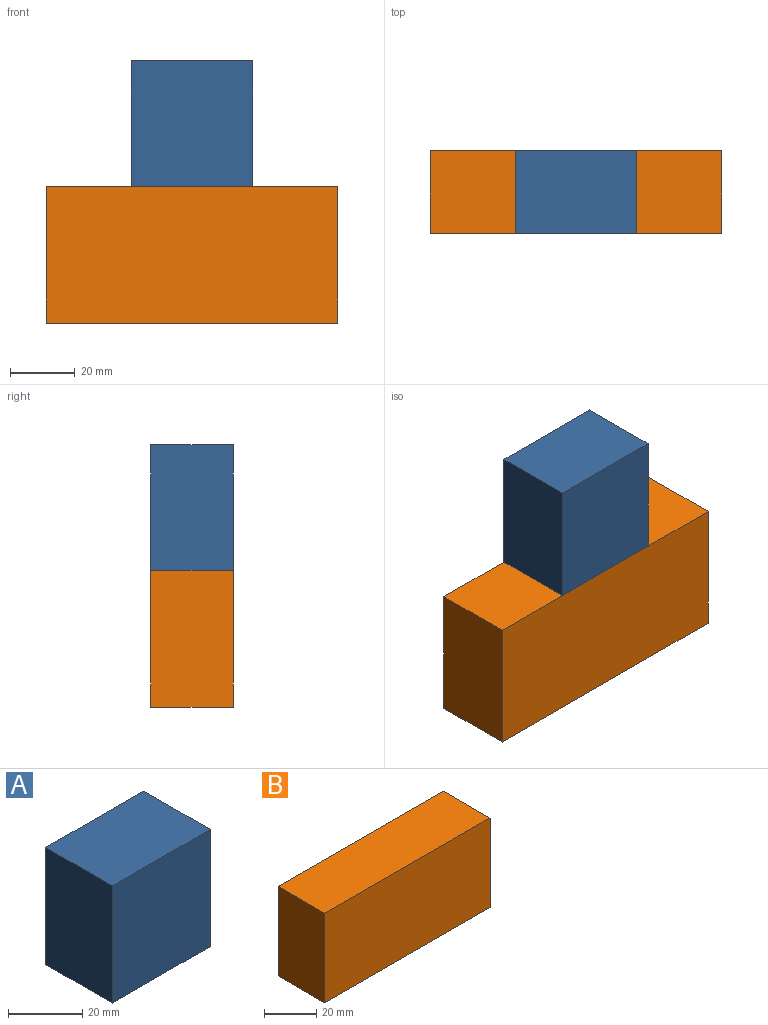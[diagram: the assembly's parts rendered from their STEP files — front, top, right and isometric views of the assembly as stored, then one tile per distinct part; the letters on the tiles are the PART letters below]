
ASSEMBLY  parts=2 mates=1
PART A: 6 faces, bbox 37.3x25.4x38.6 mm
  f0: plane 38.63x37.29mm, normal (0,-1,0), area 1440.7mm2, adj f1,f3,f4,f5
  f1: plane 38.63x25.4mm, normal (-1,0,0), area 981.3mm2, adj f0,f2,f3,f4
  f2: plane 38.63x37.29mm, normal (0,1,0), area 1440.7mm2, adj f1,f3,f4,f5
  f3: plane 37.29x25.4mm, normal (0,0,-1), area 947.2mm2, adj f0,f1,f2,f5
  f4: plane 37.29x25.4mm, normal (0,0,1), area 947.2mm2, adj f0,f1,f2,f5
  f5: plane 38.63x25.4mm, normal (1,0,0), area 981.3mm2, adj f0,f2,f3,f4
PART B: 6 faces, bbox 89.6x25.4x42.1 mm
  f0: plane 89.61x42.07mm, normal (0,-1,0), area 3769.7mm2, adj f1,f3,f4,f5
  f1: plane 42.07x25.4mm, normal (-1,0,0), area 1068.5mm2, adj f0,f2,f3,f4
  f2: plane 89.61x42.07mm, normal (0,1,0), area 3769.7mm2, adj f1,f3,f4,f5
  f3: plane 89.61x25.4mm, normal (0,0,-1), area 2276.1mm2, adj f0,f1,f2,f5
  f4: plane 89.61x25.4mm, normal (0,0,1), area 2276.1mm2, adj f0,f1,f2,f5
  f5: plane 42.07x25.4mm, normal (1,0,0), area 1068.5mm2, adj f0,f2,f3,f4
PLACE A t=(-40.25,6,59.23)mm
PLACE B t=(-37.88,6,70.13)mm
MATE parallel A.f3 <-> B.f4  axis (0,0,-1) through (-91.26,-6.7,81.56)mm
